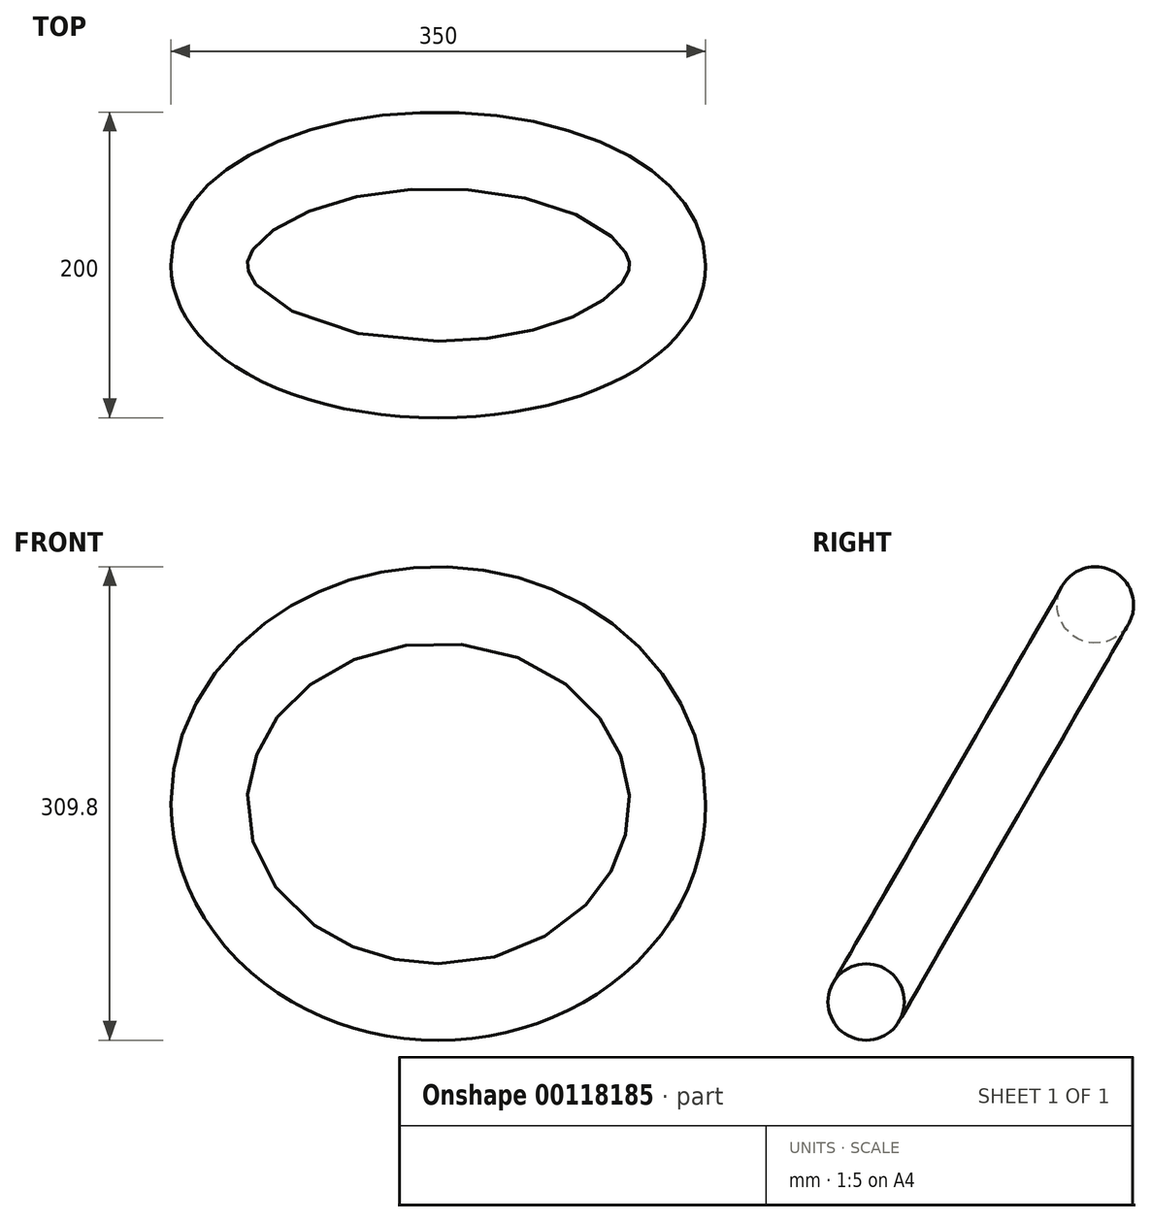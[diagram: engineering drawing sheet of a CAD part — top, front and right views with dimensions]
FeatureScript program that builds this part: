
annotation { "Feature Type Name" : "Feature", "Feature Type Description" : "" }
export const myFeature = defineFeature(function(context is Context, id is Id, definition is map)
    precondition{}
    {
        {
            var Q0;
            Q0=qCreatedBy(makeId("Front.planeOp"),FACE);
            var sketch = newSketch(context, id + "F0", { "sketchPlane" : qUnion([Q0])});
            skLineSegment(sketch, "E0", {"start": v(-76.95, 0) * mm, "end": v(78.2, 0) * mm, "construction": true});
            skSolve(sketch);
        }
        {
            var Q0;
            Q0=sQuery(id+"F0.wireOp",EDGE,"E0");
            cPlane(context, id + "F1", {"entities" : qUnion([Q0]), "cplaneType" : CPlaneType.LINE_ANGLE, "offset" : 25.4 * mm, "angle" : 240 * degree, "width" : 152.4 * mm, "height" : 152.4 * mm});
        }
        {
            var Q0;
            Q0=sQuery(id+"F0.wireOp",EDGE,"E0");
            cPlane(context, id + "F2", {"entities" : qUnion([Q0]), "cplaneType" : CPlaneType.LINE_ANGLE, "offset" : 25 * mm, "angle" : 330 * degree, "width" : 150 * mm, "height" : 150 * mm});
        }
        {
            var Q0;
            Q0=qCreatedBy(id+"F1.planeOp",FACE);
            var sketch = newSketch(context, id + "F3", { "sketchPlane" : qUnion([Q0])});
            skCircle(sketch, "E1", {"center": v(-150, 0) * mm, "radius": 25 * mm});
            skLineSegment(sketch, "E2", {"start": v(0, 96.5) * mm, "end": v(0, -87.47) * mm, "construction": true});
            skSolve(sketch);
        }
        {
            var Q0;
            Q0=makeQuery(id+"F3.imprint","IMPRINT",FACE,{"disambiguationData":[TD([[makeQuery(id+"F3.imprint","IMPRINT",EDGE,{"derivedFrom":sQuery(id+"F3.wireOp",EDGE,"E1")}),1.0]])]});
            var Q1;
            Q1=sQuery(id+"F3.wireOp",EDGE,"E2");
            revolve(context, id + "F4", {"entities" : qUnion([Q0]), "axis" : qUnion([Q1]), "revolveType" : RevolveType.FULL});
        }
        {
            var Q0;
            Q0=qCreatedBy(id+"F2.planeOp",FACE);
            cPlane(context, id + "F5", {"entities" : qUnion([Q0]), "cplaneType" : CPlaneType.OFFSET, "offset" : 30 * mm, "width" : 150 * mm, "height" : 150 * mm});
        }
    });
